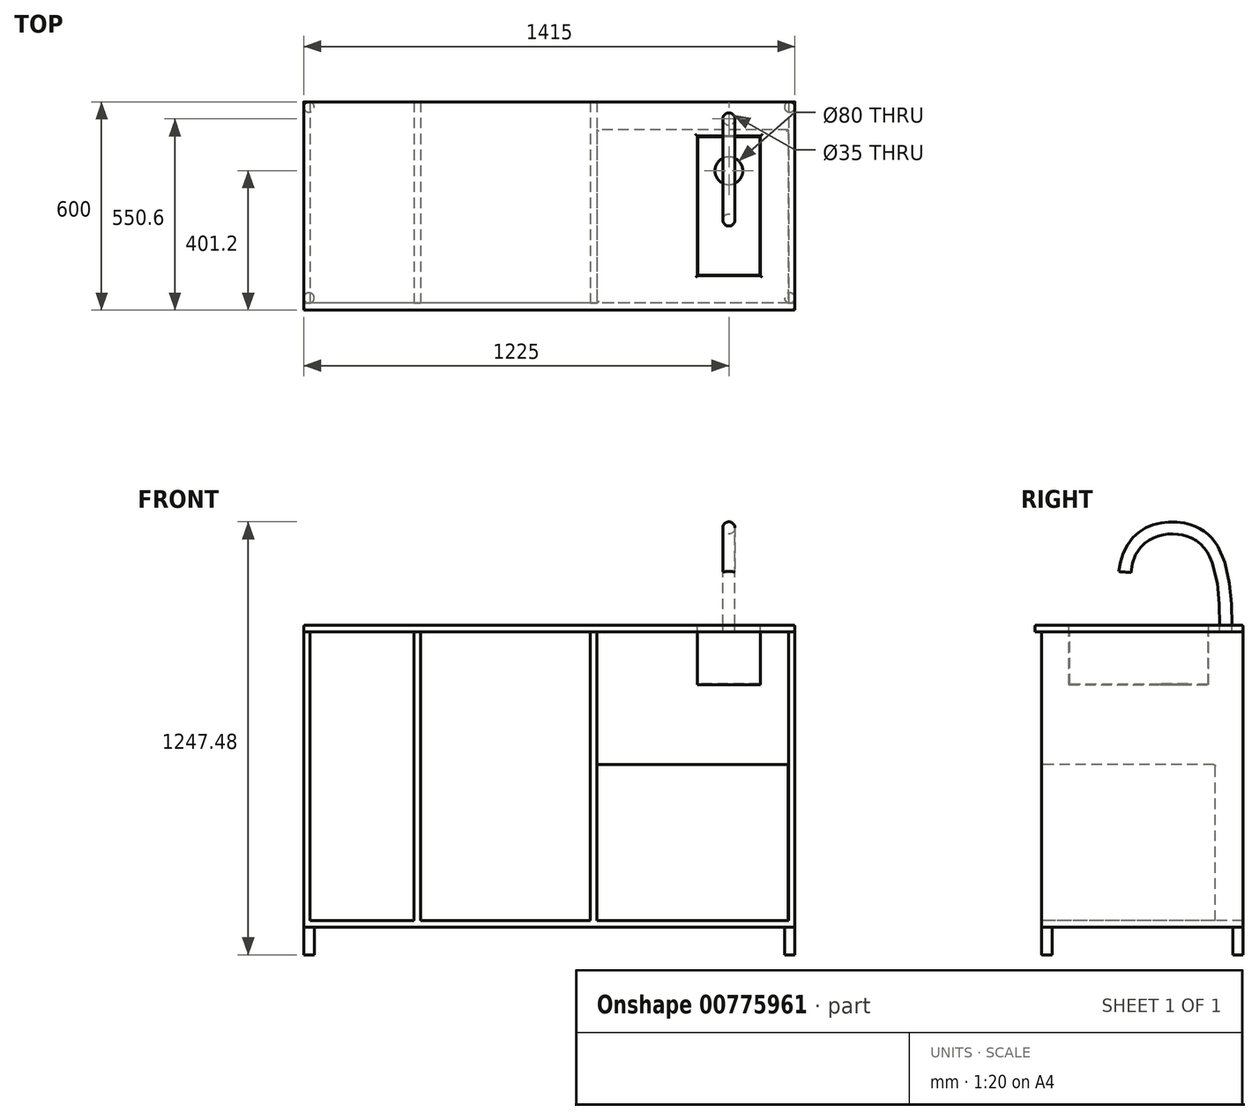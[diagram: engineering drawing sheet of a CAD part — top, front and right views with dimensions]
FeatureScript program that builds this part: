
annotation { "Feature Type Name" : "Feature", "Feature Type Description" : "" }
export const myFeature = defineFeature(function(context is Context, id is Id, definition is map)
    precondition{}
    {
        {
            assignVariable(context, id + "F0", {"name" : "dubina", "anyValue" : 20 * mm});
        }
        {
            var Q0;
            Q0=qCreatedBy(makeId("Front.planeOp"),FACE);
            var sketch = newSketch(context, id + "F1", { "sketchPlane" : qUnion([Q0])});
            skLineSegment(sketch, "E0.bottom", {"start": v(0, 0) * mm, "end": v(1415, 0) * mm});
            skLineSegment(sketch, "E0.top", {"start": v(0, -950) * mm, "end": v(1415, -950) * mm});
            skLineSegment(sketch, "E0.left", {"start": v(0, 0) * mm, "end": v(0, -950) * mm});
            skLineSegment(sketch, "E0.right", {"start": v(1415, 0) * mm, "end": v(1415, -950) * mm});
            skLineSegment(sketch, "E1.bottom", {"start": v(1415, -870) * mm, "end": v(0, -870) * mm});
            skLineSegment(sketch, "E1.top", {"start": v(1415, -852) * mm, "end": v(0, -852) * mm});
            skLineSegment(sketch, "E1.left", {"start": v(1415, -870) * mm, "end": v(1415, -852) * mm});
            skLineSegment(sketch, "E1.right", {"start": v(0, -870) * mm, "end": v(0, -852) * mm});
            skLineSegment(sketch, "E2.top", {"start": v(0, -20) * mm, "end": v(1415, -20) * mm});
            skLineSegment(sketch, "E2.left", {"start": v(0, 0) * mm, "end": v(0, -20) * mm});
            skLineSegment(sketch, "E2.right", {"start": v(1415, 0) * mm, "end": v(1415, -20) * mm});
            skLineSegment(sketch, "E3.bottom", {"start": v(0, -20) * mm, "end": v(18, -20) * mm});
            skLineSegment(sketch, "E3.top", {"start": v(0, -852) * mm, "end": v(18, -852) * mm});
            skLineSegment(sketch, "E3.left", {"start": v(0, -20) * mm, "end": v(0, -852) * mm});
            skLineSegment(sketch, "E3.right", {"start": v(18, -20) * mm, "end": v(18, -852) * mm});
            skLineSegment(sketch, "E4.bottom", {"start": v(1415, -20) * mm, "end": v(1397, -20) * mm});
            skLineSegment(sketch, "E4.top", {"start": v(1415, -852) * mm, "end": v(1397, -852) * mm});
            skLineSegment(sketch, "E4.left", {"start": v(1415, -20) * mm, "end": v(1415, -852) * mm});
            skLineSegment(sketch, "E4.right", {"start": v(1397, -20) * mm, "end": v(1397, -852) * mm});
            skLineSegment(sketch, "E5.bottom", {"start": v(826, -20) * mm, "end": v(844, -20) * mm});
            skLineSegment(sketch, "E5.top", {"start": v(826, -852) * mm, "end": v(844, -852) * mm});
            skLineSegment(sketch, "E5.left", {"start": v(826, -20) * mm, "end": v(826, -852) * mm});
            skLineSegment(sketch, "E5.right", {"start": v(844, -20) * mm, "end": v(844, -852) * mm});
            skLineSegment(sketch, "E6.bottom", {"start": v(845, -852) * mm, "end": v(1396, -852) * mm});
            skLineSegment(sketch, "E6.top", {"start": v(845, -402) * mm, "end": v(1396, -402) * mm});
            skLineSegment(sketch, "E6.left", {"start": v(845, -852) * mm, "end": v(845, -402) * mm});
            skLineSegment(sketch, "E6.right", {"start": v(1396, -852) * mm, "end": v(1396, -402) * mm});
            skPoint(sketch, "E7", {"position": v(1120.5, -852) * mm});
            skLineSegment(sketch, "E8.bottom", {"start": v(318, -20) * mm, "end": v(336, -20) * mm});
            skLineSegment(sketch, "E8.top", {"start": v(318, -852) * mm, "end": v(336, -852) * mm});
            skLineSegment(sketch, "E8.left", {"start": v(318, -20) * mm, "end": v(318, -852) * mm});
            skLineSegment(sketch, "E8.right", {"start": v(336, -20) * mm, "end": v(336, -852) * mm});
            skLineSegment(sketch, "E9.bottom", {"start": v(336, -20) * mm, "end": v(826, -20) * mm});
            skLineSegment(sketch, "E9.top", {"start": v(336, -220) * mm, "end": v(826, -220) * mm});
            skLineSegment(sketch, "E9.left", {"start": v(336, -20) * mm, "end": v(336, -220) * mm});
            skLineSegment(sketch, "E9.right", {"start": v(826, -20) * mm, "end": v(826, -220) * mm});
            skSolve(sketch);
        }
        {
            var Q0;
            {var subQ1=sQuery(id+"F1.wireOp",EDGE,"E0.bottom");Q0=makeQuery(id+"F1.imprint","IMPRINT",FACE,{"disambiguationData":[TD([[makeQuery(id+"F1.imprint","IMPRINT",EDGE,{"derivedFrom":subQ1}),-1.0]])]});}
            extrude(context, id + "F2", {"entities" : qUnion([Q0]), "oppositeDirection" : true, "depth" : 600 * mm, "offsetDistance" : 25 * mm});
        }
        {
            var Q0;
            {var subQ5=sQuery(id+"F1.wireOp",EDGE,"E3.right");Q0=makeQuery(id+"F1.imprint","IMPRINT",FACE,{"disambiguationData":[TD([[makeQuery(id+"F1.imprint","IMPRINT",EDGE,{"derivedFrom":subQ5}),-1.0]])]});}
            var Q1;
            {var subQ11=sQuery(id+"F1.wireOp",EDGE,"E1.bottom");Q1=makeQuery(id+"F1.imprint","IMPRINT",FACE,{"disambiguationData":[TD([[makeQuery(id+"F1.imprint","IMPRINT",EDGE,{"derivedFrom":subQ11}),-1.0]])]});}
            var Q2;
            {var subQ5=sQuery(id+"F1.wireOp",EDGE,"E4.right");Q2=makeQuery(id+"F1.imprint","IMPRINT",FACE,{"disambiguationData":[TD([[makeQuery(id+"F1.imprint","IMPRINT",EDGE,{"derivedFrom":subQ5}),1.0]])]});}
            var Q3;
            {var subQ6=sQuery(id+"F1.wireOp",EDGE,"E5.right");Q3=makeQuery(id+"F1.imprint","IMPRINT",FACE,{"disambiguationData":[TD([[makeQuery(id+"F1.imprint","IMPRINT",EDGE,{"derivedFrom":subQ6}),-1.0]])]});}
            var Q4;
            {var subQ4=sQuery(id+"F1.wireOp",EDGE,"E8.left");Q4=makeQuery(id+"F1.imprint","IMPRINT",FACE,{"disambiguationData":[TD([[makeQuery(id+"F1.imprint","IMPRINT",EDGE,{"derivedFrom":subQ4}),1.0]])]});}
            extrude(context, id + "F3", {"entities" : qUnion([Q0, Q1, Q2, Q3, Q4]), "oppositeDirection" : true, "depth" : 600 * mm, "offsetDistance" : 25 * mm, "hasSecondDirection" : true, "secondDirectionOppositeDirection" : true, "secondDirectionDepth" : getVariable(context, 'dubina')});
        }
        {
            var Q0;
            Q0=makeQuery(id+"F1.imprint","IMPRINT",FACE,{"disambiguationData":[TD([[makeQuery(id+"F1.imprint","IMPRINT",EDGE,{"derivedFrom":sQuery(id+"F1.wireOp",EDGE,"E6.top")}),-1.0]])]});
            extrude(context, id + "F4", {"entities" : qUnion([Q0]), "oppositeDirection" : true, "depth" : 500 * mm + getVariable(context, 'dubina'), "offsetDistance" : 25 * mm, "hasSecondDirection" : true, "secondDirectionOppositeDirection" : true, "secondDirectionDepth" : getVariable(context, 'dubina')});
        }
        {
            var Q0;
            Q0=makeQuery(id+"F3.opExtrude","SWEPT_FACE",FACE,{"disambiguationData":[OSD([sQuery(id+"F1.wireOp",EDGE,"E1.bottom")])]});
            var sketch = newSketch(context, id + "F5", { "sketchPlane" : qUnion([Q0])});
            skCircle(sketch, "E10", {"center": v(15, -35) * mm, "radius": 15 * mm});
            skCircle(sketch, "E11", {"center": v(15, -585) * mm, "radius": 15 * mm});
            skCircle(sketch, "E12", {"center": v(1400, -585) * mm, "radius": 15 * mm});
            skCircle(sketch, "E13", {"center": v(1400, -35) * mm, "radius": 15 * mm});
            skSolve(sketch);
        }
        {
            var Q0;
            Q0=makeQuery(id+"F2.opExtrude","SWEPT_FACE",FACE,{"disambiguationData":[OSD([sQuery(id+"F1.wireOp",EDGE,"E0.bottom")])]});
            var sketch = newSketch(context, id + "F6", { "sketchPlane" : qUnion([Q0])});
            skPoint(sketch, "E14", {"position": v(1415, 300) * mm});
            skLineSegment(sketch, "E15.bottom", {"start": v(1316.2, 98.8) * mm, "end": v(1133.8, 98.8) * mm});
            skLineSegment(sketch, "E15.top", {"start": v(1316.2, 501.2) * mm, "end": v(1133.8, 501.2) * mm});
            skLineSegment(sketch, "E15.left", {"start": v(1316.2, 98.8) * mm, "end": v(1316.2, 501.2) * mm});
            skLineSegment(sketch, "E15.right", {"start": v(1133.8, 98.8) * mm, "end": v(1133.8, 501.2) * mm});
            skPoint(sketch, "E15.middle", {"position": v(1225, 300) * mm});
            skLineSegment(sketch, "E16.bottom", {"start": v(1415, 0) * mm, "end": v(1316.2, 0) * mm});
            skLineSegment(sketch, "E16.top", {"start": v(1415, 98.8) * mm, "end": v(1316.2, 98.8) * mm});
            skLineSegment(sketch, "E16.left", {"start": v(1415, 0) * mm, "end": v(1415, 98.8) * mm});
            skLineSegment(sketch, "E16.right", {"start": v(1316.2, 0) * mm, "end": v(1316.2, 98.8) * mm});
            skCircle(sketch, "E17", {"center": v(1225, 550.6) * mm, "radius": 17.5 * mm});
            skLineSegment(sketch, "E18", {"start": v(1316.2, 501.2) * mm, "end": v(1316.2, 600) * mm});
            skPoint(sketch, "E19", {"position": v(1316.2, 550.6) * mm});
            skSolve(sketch);
        }
        {
            var Q0;
            Q0=makeQuery(id+"F6.imprint","IMPRINT",FACE,{"disambiguationData":[TD([[makeQuery(id+"F6.imprint","IMPRINT",EDGE,{"derivedFrom":sQuery(id+"F6.wireOp",EDGE,"E15.bottom")}),-1.0]])]});
            extrude(context, id + "F7", {"entities" : qUnion([Q0]), "operationType" : NewBodyOperationType.REMOVE, "endBound" : BoundingType.UP_TO_NEXT, "oppositeDirection" : true, "depth" : 25 * mm, "offsetDistance" : 25 * mm});
        }
        {
            var Q0;
            {var subQ0=sQuery(id+"F5.wireOp",EDGE,"E10");var subQ1=sQuery(id+"F1.wireOp",EDGE,"E1.bottom");var subQ3=makeQuery(id+"F5.imprint","INTERSECT",VERTEX,{"derivedFrom":[makeQuery(id+"F3.opExtrude","CAP_EDGE",EDGE,{"disambiguationData":[OSD([subQ1])],"isStart":true}),subQ0]});Q0=makeQuery(id+"F5.imprint","IMPRINT",FACE,{"disambiguationData":[TD([[makeQuery(id+"F5.imprint","IMPRINT",EDGE,{"disambiguationData":[TD([[subQ3,-1.0]])],"derivedFrom":subQ0}),1.0]])]});}
            var Q1;
            {var subQ0=sQuery(id+"F5.wireOp",EDGE,"E11");var subQ1=sQuery(id+"F1.wireOp",EDGE,"E1.bottom");var subQ3=makeQuery(id+"F5.imprint","INTERSECT",VERTEX,{"derivedFrom":[makeQuery(id+"F3.opExtrude","CAP_EDGE",EDGE,{"disambiguationData":[OSD([subQ1])],"isStart":false}),subQ0]});Q1=makeQuery(id+"F5.imprint","IMPRINT",FACE,{"disambiguationData":[TD([[makeQuery(id+"F5.imprint","IMPRINT",EDGE,{"disambiguationData":[TD([[subQ3,1.0]])],"derivedFrom":subQ0}),1.0]])]});}
            var Q2;
            {var subQ0=sQuery(id+"F5.wireOp",EDGE,"E12");var subQ1=sQuery(id+"F1.wireOp",EDGE,"E1.bottom");var subQ3=makeQuery(id+"F5.imprint","INTERSECT",VERTEX,{"derivedFrom":[makeQuery(id+"F3.opExtrude","CAP_EDGE",EDGE,{"disambiguationData":[OSD([subQ1])],"isStart":false}),subQ0]});Q2=makeQuery(id+"F5.imprint","IMPRINT",FACE,{"disambiguationData":[TD([[makeQuery(id+"F5.imprint","IMPRINT",EDGE,{"disambiguationData":[TD([[subQ3,1.0]])],"derivedFrom":subQ0}),1.0]])]});}
            var Q3;
            {var subQ0=sQuery(id+"F5.wireOp",EDGE,"E13");var subQ1=sQuery(id+"F1.wireOp",EDGE,"E1.bottom");var subQ3=makeQuery(id+"F5.imprint","INTERSECT",VERTEX,{"derivedFrom":[makeQuery(id+"F3.opExtrude","CAP_EDGE",EDGE,{"disambiguationData":[OSD([subQ1])],"isStart":true}),subQ0]});Q3=makeQuery(id+"F5.imprint","IMPRINT",FACE,{"disambiguationData":[TD([[makeQuery(id+"F5.imprint","IMPRINT",EDGE,{"disambiguationData":[TD([[subQ3,1.0]])],"derivedFrom":subQ0}),1.0]])]});}
            var Q4;
            Q4=sQuery(id+"F1.wireOp",VERTEX,"E0.top.end");
            extrude(context, id + "F8", {"entities" : qUnion([Q0, Q1, Q2, Q3]), "operationType" : NewBodyOperationType.ADD, "endBound" : BoundingType.UP_TO_VERTEX, "depth" : 25 * mm, "endBoundEntityVertex" : qUnion([Q4]), "offsetDistance" : 25 * mm});
        }
        {
            var Q0;
            Q0=makeQuery(id+"F2.opExtrude","SWEPT_FACE",FACE,{"disambiguationData":[OSD([sQuery(id+"F1.wireOp",EDGE,"E2.top")])]});
            var sketch = newSketch(context, id + "F9", { "sketchPlane" : qUnion([Q0])});
            skLineSegment(sketch, "E20.bottom", {"start": v(1316.2, -501.2) * mm, "end": v(1133.8, -501.2) * mm});
            skLineSegment(sketch, "E20.top", {"start": v(1316.2, -98.8) * mm, "end": v(1133.8, -98.8) * mm});
            skLineSegment(sketch, "E20.left", {"start": v(1316.2, -501.2) * mm, "end": v(1316.2, -98.8) * mm});
            skLineSegment(sketch, "E20.right", {"start": v(1133.8, -501.2) * mm, "end": v(1133.8, -98.8) * mm});
            skPoint(sketch, "E20.middle", {"position": v(1225, -300) * mm});
            skSolve(sketch);
        }
        {
            var Q0;
            Q0 = qSketchRegion(id + "F9", true);
            extrude(context, id + "F10", {"entities" : qUnion([Q0]), "depth" : 152 * mm, "offsetDistance" : 25 * mm});
        }
        {
            var Q0;
            Q0=makeQuery(id+"F10.opExtrude","CAP_FACE",FACE,{"disambiguationData":[OSD([sQuery(id+"F9.wireOp",EDGE,"E20.bottom"),sQuery(id+"F9.wireOp",EDGE,"E20.top"),sQuery(id+"F9.wireOp",EDGE,"E20.left"),sQuery(id+"F9.wireOp",EDGE,"E20.right")])],"isStart":true});
            shell(context, id + "F11", {"entities" : qUnion([Q0]), "thickness" : 2 * mm});
        }
        {
            var Q0;
            Q0=makeQuery(id+"F6.imprint","IMPRINT",FACE,{"disambiguationData":[TD([[makeQuery(id+"F6.imprint","IMPRINT",EDGE,{"derivedFrom":sQuery(id+"F6.wireOp",EDGE,"E17")}),1.0]])]});
            extrude(context, id + "F12", {"entities" : qUnion([Q0]), "operationType" : NewBodyOperationType.REMOVE, "endBound" : BoundingType.UP_TO_NEXT, "oppositeDirection" : true, "depth" : 25 * mm, "offsetDistance" : 25 * mm});
        }
        {
            var Q0;
            Q0=qCreatedBy(makeId("Right.planeOp"),FACE);
            var Q1;
            Q1=sQuery(id+"F6.wireOp",VERTEX,"E17.center");
            cPlane(context, id + "F13", {"entities" : qUnion([Q0, Q1]), "cplaneType" : CPlaneType.PLANE_POINT, "offset" : 25 * mm, "width" : 150 * mm, "height" : 150 * mm});
        }
        {
            var Q0;
            Q0=qCreatedBy(id+"F13.planeOp",FACE);
            var sketch = newSketch(context, id + "F14", { "sketchPlane" : qUnion([Q0])});
            skFitSpline(sketch, "E21", {"points": [v(550.1, 0) * mm, v(460.4, 265.37) * mm, v(260.11, 152.61) * mm], "startDerivative": vector(-2.58, 703) * mm, "endDerivative": vector(-61.2, -783.55) * mm});
            skSolve(sketch);
        }
        {
            var Q0;
            Q0=makeQuery(id+"F6.imprint","IMPRINT",FACE,{"disambiguationData":[TD([[makeQuery(id+"F6.imprint","IMPRINT",EDGE,{"derivedFrom":sQuery(id+"F6.wireOp",EDGE,"E17")}),1.0]])]});
            var Q1;
            Q1=sQuery(id+"F14.wireOp",EDGE,"E21");
            sweep(context, id + "F15", {"profiles" : qUnion([Q0]), "path" : qUnion([Q1])});
        }
        {
            var Q0;
            Q0=makeQuery(id+"F10.opExtrude","CAP_FACE",FACE,{"disambiguationData":[OSD([sQuery(id+"F9.wireOp",EDGE,"E20.bottom"),sQuery(id+"F9.wireOp",EDGE,"E20.top"),sQuery(id+"F9.wireOp",EDGE,"E20.left"),sQuery(id+"F9.wireOp",EDGE,"E20.right")])],"isStart":false});
            var sketch = newSketch(context, id + "F16", { "sketchPlane" : qUnion([Q0])});
            skCircle(sketch, "E22", {"center": v(1225, -401.2) * mm, "radius": 40 * mm});
            skPoint(sketch, "E23", {"position": v(1225, -501.2) * mm});
            skSolve(sketch);
        }
        {
            var Q0;
            Q0=sQuery(id+"F16.wireOp",VERTEX,"E22.center");
            var Q1;
            Q1=makeQuery(id+"F10.opExtrude","SWEPT_BODY",BODY,{"disambiguationData":[OSD([sQuery(id+"F9.wireOp",EDGE,"E20.bottom"),sQuery(id+"F9.wireOp",EDGE,"E20.top"),sQuery(id+"F9.wireOp",EDGE,"E20.left"),sQuery(id+"F9.wireOp",EDGE,"E20.right")])]});
            hole(context, id + "F17", {"style" : HoleStyle.SIMPLE, "endStyle" : HoleEndStyle.THROUGH, "holeDiameter" : 80 * mm, "majorDiameter" : 5 * mm, "isTappedThrough" : true, "tappedDepth" : 12 * mm, "tapClearance" : 3, "locations" : qUnion([Q0]), "scope" : qUnion([Q1])});
        }
        {
            var Q0;
            Q0=makeQuery(id+"F2.opExtrude","SWEPT_FACE",FACE,{"disambiguationData":[OSD([sQuery(id+"F1.wireOp",EDGE,"E0.bottom")])]});
            fillet(context, id + "F18", {"entities" : qUnion([Q0]), "radius" : 5 * mm, "tangentPropagation" : true, "allowEdgeOverflow" : false});
        }
        {
            var Q0;
            Q0=makeQuery(id+"F4.opExtrude","SWEPT_FACE",FACE,{"disambiguationData":[OSD([sQuery(id+"F1.wireOp",EDGE,"E6.top")])]});
            fillet(context, id + "F19", {"entities" : qUnion([Q0]), "radius" : 5 * mm, "tangentPropagation" : true, "allowEdgeOverflow" : false});
        }
    });
